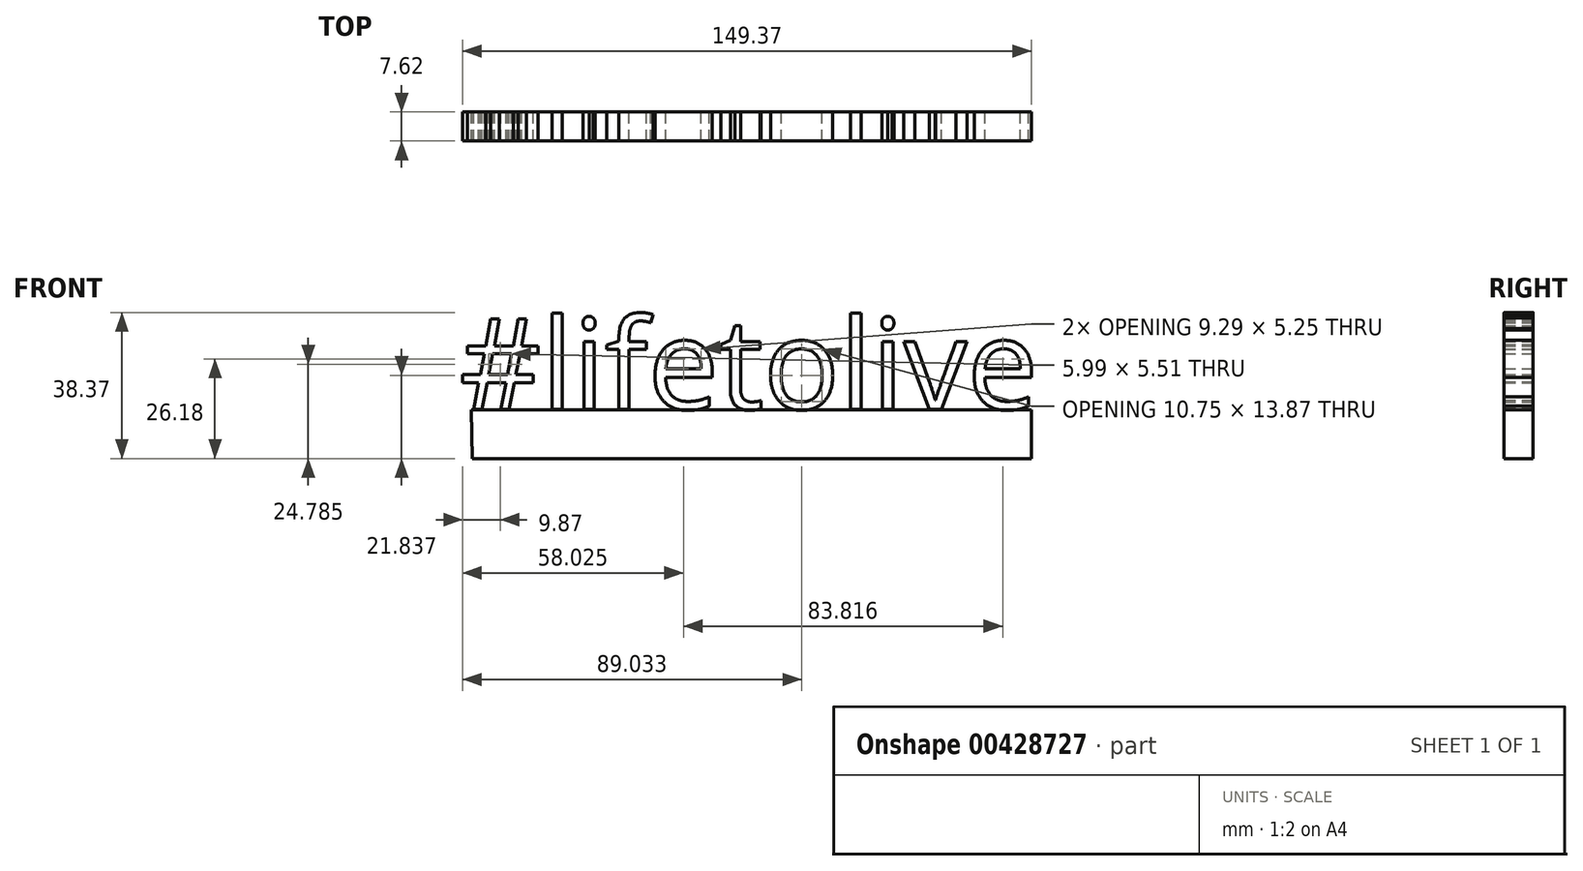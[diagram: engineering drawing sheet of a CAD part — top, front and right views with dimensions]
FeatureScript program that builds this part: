
annotation { "Feature Type Name" : "Feature", "Feature Type Description" : "" }
export const myFeature = defineFeature(function(context is Context, id is Id, definition is map)
    precondition{}
    {
        {
            var Q0;
            Q0=qCreatedBy(makeId("Front.planeOp"),FACE);
            var sketch = newSketch(context, id + "F0", { "sketchPlane" : qUnion([Q0])});
            skText(sketch, "E0", { "text": "#lifetolive", "fontName": "OpenSans-Regular.ttf"});
            const initialGuessF0  = {"E0": [-0.07777, -0.01355, 1, 0, 0.0239]};
            skSetInitialGuess(sketch, initialGuessF0);
            skSolve(sketch);
        }
        {
            var Q0;
            Q0 = qSketchRegion(id + "F0", true);
            extrude(context, id + "F1", {"entities" : qUnion([Q0]), "depth" : 7.62 * mm});
        }
        {
            var Q0;
            Q0=qCreatedBy(makeId("Front.planeOp"),FACE);
            var sketch = newSketch(context, id + "F2", { "sketchPlane" : qUnion([Q0])});
            skLineSegment(sketch, "E1", {"start": v(-74.62, -13.74) * mm, "end": v(72.42, -13.74) * mm});
            skLineSegment(sketch, "E2", {"start": v(72.42, -13.74) * mm, "end": v(72.42, -26.52) * mm});
            skLineSegment(sketch, "E3", {"start": v(72.42, -26.52) * mm, "end": v(-74.43, -26.52) * mm});
            skLineSegment(sketch, "E4", {"start": v(-74.43, -26.52) * mm, "end": v(-74.62, -13.74) * mm});
            skSolve(sketch);
        }
        {
            var Q0;
            Q0=makeQuery(id+"F2.imprint","IMPRINT",FACE,{"disambiguationData":[TD([[makeQuery(id+"F2.imprint","IMPRINT",EDGE,{"derivedFrom":sQuery(id+"F2.wireOp",EDGE,"E1")}),-1.0]])]});
            extrude(context, id + "F3", {"entities" : qUnion([Q0]), "depth" : 7.62 * mm});
        }
    });
